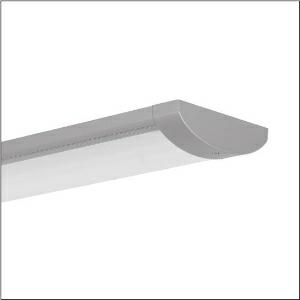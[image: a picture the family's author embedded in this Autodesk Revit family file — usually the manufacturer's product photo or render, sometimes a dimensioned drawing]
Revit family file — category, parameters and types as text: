
# Revit family: tv_20_5xa86174n0x
name_source: partatom
category: Lighting Fixtures
units: mm (PartAtom-declared; Revit-internal decimal feet)

## family parameters
Cut with Voids When Loaded = No
Host = Face
Light Source = No
Part Type = Normal
Room Calculation Point = No
Round Connector Dimension = Use Diameter
Shared = No

## types (1)
- TV 20 (1 x LED 4000K / CRI = 80 (unbekannt), 5120 lm, 4000K)
    Apparent Load = 50 VA
    CIE Flux Codes = 48 78 95 99 100
    Color Rendering = 80
    Color Temperature = 4000K
    Default Elevation = 1800 mm
    Description = TV 20, vandal-proof luminaire, primary light control with specular reflector, of aluminium, matt, primary optical cover: enclosure, of PC, frosted, light emission: direct distribution, primary light characteristic: symmetric, installation type: surface-mounted, LED, rated luminous flux: 5.120lm, luminous efficacy: 102lm/W, light colour: 840, colour temperature: 4000K, control gear: ON/OFF, mains connection: 230V, AC, 50Hz, rated input power: 50W, luminaire housing, of aluminium, coated, Siteco® metallic grey (DB 702S), with wall and ceiling fixing element, length: 1.561mm, width: 260mm, height: 70mm, mounting height: 2.5..4.0m, protection rating (complete): IP65, insulation class (complete): insulation class I (protective earthing), certification: CE, protection symbol: F, impact resistance: 2x IK10, standard: EN 60598, packaging unit: 1 piece
    Height = 70 mm
    Lamp = 1 x LED 4000K / CRI >= 80 (unbekannt)
    Lamp Light Flux = 5120 lm
    Lamp count = 1
    Length = 1561 mm
    Luminous efficacy = 102 lm/W
    Manufacturer = Siteco
    ModVariant = No
    Model = 5XA86174N0X
    Mounting Place = Ceiling
    Mounting Type = Surface mounted
    Number of Poles = 1
    OnlyDefault = Yes
    Power Factor = 1
    Product Name = TV 20
    Product group = vandal-proof luminaire
    ProductGroupID = 310
    Protection Class = Protection class I
    Protection Degree = IP 65
    RLX_Detail_Level = 1
    RLX_Emergency_Light_Flux = 0 lm
    RLX_Emergency_Type = 0
    RLX_Emergency_Type_DB = No
    RlxData = <blob elided: 25321 chars, md5=8eda4238>
    Socket = socket
    Standby Power = 0 W
    System Light Flux = 5120 lm
    System Power = 50 W
    Type Comments = Product without accessories
    Type Image = l_1004809.jpg
    URL = http://relux.com
    VarID = ---
    Voltage = 0 V
    Weight = 0.00 kg
    Width = 260 mm

## geometry (parser evidence)
native form markers: Blend x4, Sweep x12
no freeform markers — native parametric forms only
